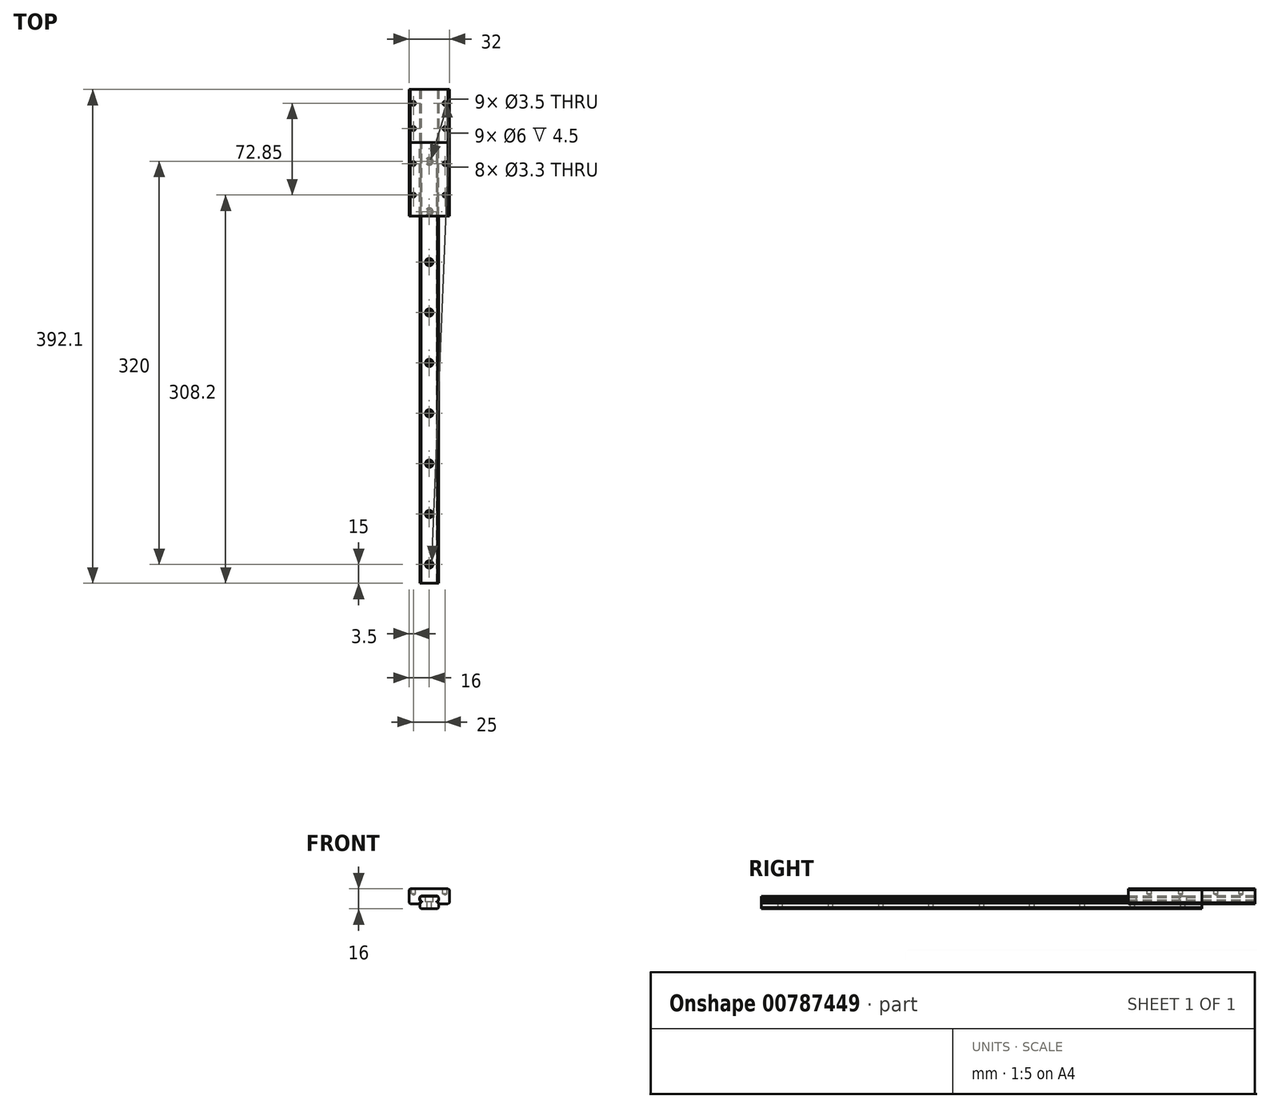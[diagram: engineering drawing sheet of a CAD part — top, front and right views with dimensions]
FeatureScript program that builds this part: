
annotation { "Feature Type Name" : "Feature", "Feature Type Description" : "" }
export const myFeature = defineFeature(function(context is Context, id is Id, definition is map)
    precondition{}
    {
        {
            var Q0;
            Q0=qCreatedBy(makeId("Front.planeOp"),FACE);
            var sketch = newSketch(context, id + "F0", { "sketchPlane" : qUnion([Q0])});
            skLineSegment(sketch, "E0.bottom", {"start": v(6.5, -5) * mm, "end": v(-6.5, -5) * mm});
            skLineSegment(sketch, "E0.top", {"start": v(6.5, 5) * mm, "end": v(-6.5, 5) * mm});
            skLineSegment(sketch, "E0.left", {"start": v(7.5, -4) * mm, "end": v(7.5, -0.41) * mm});
            skLineSegment(sketch, "E0.right", {"start": v(-7.5, -4) * mm, "end": v(-7.5, -0.41) * mm});
            skPoint(sketch, "E0.middle", {"position": v(0, 0) * mm});
            skLineSegment(sketch, "E1", {"start": v(0, 12.36) * mm, "end": v(0, -9.73) * mm, "construction": true});
            skLineSegment(sketch, "E2", {"start": v(-7.5, 2) * mm, "end": v(-6.8, 1.3) * mm});
            skLineSegment(sketch, "E3", {"start": v(-6.8, 1.3) * mm, "end": v(-5.8, 1.3) * mm});
            skLineSegment(sketch, "E4", {"start": v(-5.8, 1.3) * mm, "end": v(-5.8, 0.3) * mm});
            skLineSegment(sketch, "E5", {"start": v(-5.8, 0.3) * mm, "end": v(-6.8, 0.3) * mm});
            skLineSegment(sketch, "E6", {"start": v(-6.8, 0.3) * mm, "end": v(-7.5, -0.41) * mm});
            skLineSegment(sketch, "E7.MirrorCS", {"start": v(5.8, 0.3) * mm, "end": v(6.8, 0.3) * mm});
            skLineSegment(sketch, "E8.MirrorCS", {"start": v(6.8, 0.3) * mm, "end": v(7.5, -0.41) * mm});
            skLineSegment(sketch, "E9.MirrorCS", {"start": v(5.8, 1.3) * mm, "end": v(5.8, 0.3) * mm});
            skLineSegment(sketch, "E10.MirrorCS", {"start": v(7.5, 2) * mm, "end": v(6.8, 1.3) * mm});
            skLineSegment(sketch, "E11.MirrorCS", {"start": v(6.8, 1.3) * mm, "end": v(5.8, 1.3) * mm});
            skLineSegment(sketch, "E12.trimOffspring", {"start": v(-7.5, 2) * mm, "end": v(-7.5, 4) * mm});
            skLineSegment(sketch, "E13.trimOffspring", {"start": v(7.5, 2) * mm, "end": v(7.5, 4) * mm});
            skLineSegment(sketch, "E14", {"start": v(-7.5, 4) * mm, "end": v(-6.5, 5) * mm});
            skLineSegment(sketch, "E15.MirrorCS", {"start": v(7.5, 4) * mm, "end": v(6.5, 5) * mm});
            skLineSegment(sketch, "E16.MirrorCS", {"start": v(-7.5, -4) * mm, "end": v(-6.5, -5) * mm});
            skLineSegment(sketch, "E17.MirrorCS", {"start": v(7.5, -4) * mm, "end": v(6.5, -5) * mm});
            skPoint(sketch, "E18.orphan", {"position": v(-7.5, 5) * mm});
            skPoint(sketch, "E19.orphan", {"position": v(7.5, 5) * mm});
            skPoint(sketch, "E20.orphan", {"position": v(7.5, -5) * mm});
            skPoint(sketch, "E21.orphan", {"position": v(-7.5, -5) * mm});
            skSolve(sketch);
        }
        {
            var Q0;
            Q0=makeQuery(id+"F0.imprint","IMPRINT",FACE,{"disambiguationData":[TD([[makeQuery(id+"F0.imprint","IMPRINT",EDGE,{"derivedFrom":sQuery(id+"F0.wireOp",EDGE,"E0.bottom")}),-1.0]])]});
            extrude(context, id + "F1", {"entities" : qUnion([Q0]), "depth" : 350 * mm, "offsetDistance" : 25 * mm});
        }
        {
            var Q0;
            Q0=makeQuery(id+"F1.opExtrude","SWEPT_FACE",FACE,{"disambiguationData":[OSD([sQuery(id+"F0.wireOp",EDGE,"E0.top")])]});
            var sketch = newSketch(context, id + "F2", { "sketchPlane" : qUnion([Q0])});
            skLineSegment(sketch, "E22", {"start": v(0, 4.61) * mm, "end": v(0, -375.08) * mm, "construction": true});
            skCircle(sketch, "E23", {"center": v(0, -15) * mm, "radius": 1.75 * mm});
            skCircle(sketch, "E24.1.0.0", {"center": v(0, -55) * mm, "radius": 1.75 * mm});
            skCircle(sketch, "E24.2.0.0", {"center": v(0, -95) * mm, "radius": 1.75 * mm});
            skCircle(sketch, "E24.3.0.0", {"center": v(0, -135) * mm, "radius": 1.75 * mm});
            skCircle(sketch, "E24.4.0.0", {"center": v(0, -175) * mm, "radius": 1.75 * mm});
            skCircle(sketch, "E24.5.0.0", {"center": v(0, -215) * mm, "radius": 1.75 * mm});
            skCircle(sketch, "E24.6.0.0", {"center": v(0, -255) * mm, "radius": 1.75 * mm});
            skCircle(sketch, "E24.7.0.0", {"center": v(0, -295) * mm, "radius": 1.75 * mm});
            skCircle(sketch, "E24.8.0.0", {"center": v(0, -335) * mm, "radius": 1.75 * mm});
            skLineSegment(sketch, "E24.direction1", {"start": v(0, -15) * mm, "end": v(0, -55) * mm, "construction": true});
            skSolve(sketch);
        }
        {
            var Q0;
            Q0 = qSketchRegion(id + "F2", true);
            extrude(context, id + "F3", {"entities" : qUnion([Q0]), "operationType" : NewBodyOperationType.REMOVE, "endBound" : BoundingType.THROUGH_ALL, "oppositeDirection" : true, "depth" : 25 * mm, "offsetDistance" : 25 * mm});
        }
        {
            var Q0;
            Q0=makeQuery(id+"F1.opExtrude","SWEPT_FACE",FACE,{"disambiguationData":[OSD([sQuery(id+"F0.wireOp",EDGE,"E0.top")])]});
            var sketch = newSketch(context, id + "F4", { "sketchPlane" : qUnion([Q0])});
            skLineSegment(sketch, "E25", {"start": v(0, 167.82) * mm, "end": v(0, -211.88) * mm, "construction": true});
            skCircle(sketch, "E26", {"center": v(0, -15) * mm, "radius": 3 * mm});
            skCircle(sketch, "E27.1.0.0", {"center": v(0, -55) * mm, "radius": 3 * mm});
            skCircle(sketch, "E27.2.0.0", {"center": v(0, -95) * mm, "radius": 3 * mm});
            skCircle(sketch, "E27.3.0.0", {"center": v(0, -135) * mm, "radius": 3 * mm});
            skCircle(sketch, "E27.4.0.0", {"center": v(0, -175) * mm, "radius": 3 * mm});
            skCircle(sketch, "E27.5.0.0", {"center": v(0, -215) * mm, "radius": 3 * mm});
            skCircle(sketch, "E27.6.0.0", {"center": v(0, -255) * mm, "radius": 3 * mm});
            skCircle(sketch, "E27.7.0.0", {"center": v(0, -295) * mm, "radius": 3 * mm});
            skCircle(sketch, "E27.8.0.0", {"center": v(0, -335) * mm, "radius": 3 * mm});
            skLineSegment(sketch, "E27.direction1", {"start": v(0, -15) * mm, "end": v(0, -55) * mm, "construction": true});
            skSolve(sketch);
        }
        {
            var Q0;
            Q0 = qSketchRegion(id + "F4", true);
            extrude(context, id + "F5", {"entities" : qUnion([Q0]), "operationType" : NewBodyOperationType.REMOVE, "oppositeDirection" : true, "depth" : 4.5 * mm, "offsetDistance" : 25 * mm});
        }
        {
            var Q0;
            Q0=qCreatedBy(makeId("Front.planeOp"),FACE);
            var sketch = newSketch(context, id + "F6", { "sketchPlane" : qUnion([Q0])});
            skLineSegment(sketch, "E28", {"start": v(-7.65, -1) * mm, "end": v(-15, -1) * mm});
            skLineSegment(sketch, "E29", {"start": v(-16, 0) * mm, "end": v(-16, 10) * mm});
            skLineSegment(sketch, "E30", {"start": v(-15, 11) * mm, "end": v(0, 11) * mm});
            skLineSegment(sketch, "E31", {"start": v(-7.65, -1) * mm, "end": v(-7.65, -0.35) * mm});
            skLineSegment(sketch, "E32", {"start": v(-7.65, -0.35) * mm, "end": v(-6.8, 0.5) * mm});
            skLineSegment(sketch, "E33", {"start": v(-6.8, 0.5) * mm, "end": v(-6.8, 1.08) * mm});
            skLineSegment(sketch, "E34", {"start": v(-6.8, 1.08) * mm, "end": v(-7.65, 1.94) * mm});
            skLineSegment(sketch, "E35", {"start": v(-7.65, 1.94) * mm, "end": v(-7.65, 4.06) * mm});
            skLineSegment(sketch, "E36", {"start": v(-7.65, 4.06) * mm, "end": v(-6.56, 5.15) * mm});
            skLineSegment(sketch, "E37", {"start": v(-6.56, 5.15) * mm, "end": v(0, 5.15) * mm});
            skLineSegment(sketch, "E38", {"start": v(-16, 10) * mm, "end": v(-15, 11) * mm});
            skLineSegment(sketch, "E39", {"start": v(-15, -1) * mm, "end": v(-16, 0) * mm});
            skPoint(sketch, "E40.orphan", {"position": v(-16, -1) * mm});
            skPoint(sketch, "E41.orphan", {"position": v(-16, 11) * mm});
            skLineSegment(sketch, "E42.MirrorCS", {"start": v(15, 11) * mm, "end": v(0, 11) * mm});
            skLineSegment(sketch, "E43.MirrorCS", {"start": v(16, 10) * mm, "end": v(15, 11) * mm});
            skLineSegment(sketch, "E44.MirrorCS", {"start": v(16, 0) * mm, "end": v(16, 10) * mm});
            skLineSegment(sketch, "E45.MirrorCS", {"start": v(15, -1) * mm, "end": v(16, 0) * mm});
            skLineSegment(sketch, "E46.MirrorCS", {"start": v(7.65, -1) * mm, "end": v(15, -1) * mm});
            skLineSegment(sketch, "E47.MirrorCS", {"start": v(7.65, -1) * mm, "end": v(7.65, -0.35) * mm});
            skLineSegment(sketch, "E48.MirrorCS", {"start": v(7.65, -0.35) * mm, "end": v(6.8, 0.5) * mm});
            skLineSegment(sketch, "E49.MirrorCS", {"start": v(6.8, 0.5) * mm, "end": v(6.8, 1.08) * mm});
            skLineSegment(sketch, "E50.MirrorCS", {"start": v(6.8, 1.08) * mm, "end": v(7.65, 1.94) * mm});
            skLineSegment(sketch, "E51.MirrorCS", {"start": v(7.65, 1.94) * mm, "end": v(7.65, 4.06) * mm});
            skLineSegment(sketch, "E52.MirrorCS", {"start": v(7.65, 4.06) * mm, "end": v(6.56, 5.15) * mm});
            skLineSegment(sketch, "E53.MirrorCS", {"start": v(6.56, 5.15) * mm, "end": v(0, 5.15) * mm});
            skSolve(sketch);
        }
        {
            var Q0;
            Q0 = qSketchRegion(id + "F6", true);
            extrude(context, id + "F7", {"entities" : qUnion([Q0]), "depth" : 58.6 * mm, "offsetDistance" : 25 * mm});
        }
        {
            var Q0;
            Q0 = qSketchRegion(id + "F6", true);
            extrude(context, id + "F8", {"entities" : qUnion([Q0]), "oppositeDirection" : true, "depth" : 42.1 * mm, "offsetDistance" : 25 * mm});
        }
        {
            var Q0;
            Q0=makeQuery(id+"F7.opExtrude","SWEPT_FACE",FACE,{"disambiguationData":[OSD([sQuery(id+"F6.wireOp",EDGE,"E30"),sQuery(id+"F6.wireOp",EDGE,"E42.MirrorCS")])]});
            var sketch = newSketch(context, id + "F9", { "sketchPlane" : qUnion([Q0])});
            skLineSegment(sketch, "E54", {"start": v(-15, 0) * mm, "end": v(15, -58.6) * mm, "construction": true});
            skLineSegment(sketch, "E55", {"start": v(15, 0) * mm, "end": v(-15, -58.6) * mm, "construction": true});
            skLineSegment(sketch, "E56", {"start": v(-37.81, -29.3) * mm, "end": v(32.35, -29.3) * mm, "construction": true});
            skPoint(sketch, "E56.startSnap0", {"position": v(0, -29.3) * mm});
            skLineSegment(sketch, "E57", {"start": v(0, 0) * mm, "end": v(0, -61.52) * mm, "construction": true});
            skCircle(sketch, "E58", {"center": v(-12.5, -16.8) * mm, "radius": 1.5 * mm});
            skCircle(sketch, "E59.MirrorC", {"center": v(12.5, -16.8) * mm, "radius": 1.5 * mm});
            skCircle(sketch, "E60.MirrorC", {"center": v(-12.5, -41.8) * mm, "radius": 1.5 * mm});
            skCircle(sketch, "E61.MirrorC", {"center": v(12.5, -41.8) * mm, "radius": 1.5 * mm});
            skSolve(sketch);
        }
        {
            var Q0;
            Q0=makeQuery(id+"F8.opExtrude","SWEPT_FACE",FACE,{"disambiguationData":[OSD([sQuery(id+"F6.wireOp",EDGE,"E30"),sQuery(id+"F6.wireOp",EDGE,"E42.MirrorCS")])]});
            var sketch = newSketch(context, id + "F10", { "sketchPlane" : qUnion([Q0])});
            skLineSegment(sketch, "E62", {"start": v(-34.35, 21.05) * mm, "end": v(28.23, 21.05) * mm, "construction": true});
            skLineSegment(sketch, "E63", {"start": v(0, 49.38) * mm, "end": v(0, -1.77) * mm, "construction": true});
            skCircle(sketch, "E64", {"center": v(-12.5, 31.05) * mm, "radius": 1.5 * mm});
            skCircle(sketch, "E65.MirrorC", {"center": v(12.5, 31.05) * mm, "radius": 1.5 * mm});
            skCircle(sketch, "E66.MirrorC", {"center": v(-12.5, 11.05) * mm, "radius": 1.5 * mm});
            skCircle(sketch, "E67.MirrorC", {"center": v(12.5, 11.05) * mm, "radius": 1.5 * mm});
            skSolve(sketch);
        }
        {
            var Q0;
            Q0=sQuery(id+"F9.wireOp",VERTEX,"E58.center");
            var Q1;
            Q1=sQuery(id+"F9.wireOp",VERTEX,"E59.MirrorC.center");
            var Q2;
            Q2=sQuery(id+"F9.wireOp",VERTEX,"E60.MirrorC.center");
            var Q3;
            Q3=sQuery(id+"F9.wireOp",VERTEX,"E61.MirrorC.center");
            var Q4;
            Q4=makeQuery(id+"F7.opExtrude","SWEPT_BODY",BODY,{"disambiguationData":[OSD([sQuery(id+"F6.wireOp",EDGE,"E28"),sQuery(id+"F6.wireOp",EDGE,"E29"),sQuery(id+"F6.wireOp",EDGE,"E30"),sQuery(id+"F6.wireOp",EDGE,"E31"),sQuery(id+"F6.wireOp",EDGE,"E32"),sQuery(id+"F6.wireOp",EDGE,"E33"),sQuery(id+"F6.wireOp",EDGE,"E34"),sQuery(id+"F6.wireOp",EDGE,"E35"),sQuery(id+"F6.wireOp",EDGE,"E36"),sQuery(id+"F6.wireOp",EDGE,"E37"),sQuery(id+"F6.wireOp",EDGE,"E38"),sQuery(id+"F6.wireOp",EDGE,"E39"),sQuery(id+"F6.wireOp",EDGE,"E42.MirrorCS"),sQuery(id+"F6.wireOp",EDGE,"E43.MirrorCS"),sQuery(id+"F6.wireOp",EDGE,"E44.MirrorCS"),sQuery(id+"F6.wireOp",EDGE,"E45.MirrorCS"),sQuery(id+"F6.wireOp",EDGE,"E46.MirrorCS"),sQuery(id+"F6.wireOp",EDGE,"E47.MirrorCS"),sQuery(id+"F6.wireOp",EDGE,"E48.MirrorCS"),sQuery(id+"F6.wireOp",EDGE,"E49.MirrorCS"),sQuery(id+"F6.wireOp",EDGE,"E50.MirrorCS"),sQuery(id+"F6.wireOp",EDGE,"E51.MirrorCS"),sQuery(id+"F6.wireOp",EDGE,"E52.MirrorCS"),sQuery(id+"F6.wireOp",EDGE,"E53.MirrorCS")])]});
            hole(context, id + "F11", {"style" : HoleStyle.SIMPLE, "endStyle" : HoleEndStyle.BLIND, "standardTappedOrClearance" : lookupTablePath({ "standard" : "ISO", "fit" : "Normal", "size" : "M3", "type" : "Clearance" }), "standardBlindInLast" : lookupTablePath({ "fit" : "Standard", "standard" : "ISO", "size" : "M3", "type" : "Clearance" }), "holeDiameter" : 3.3 * mm, "majorDiameter" : 5 * mm, "holeDepth" : 4 * mm, "isTappedThrough" : true, "tappedDepth" : 12 * mm, "tapClearance" : 3, "startFromSketch" : true, "locations" : qUnion([Q0, Q1, Q2, Q3]), "scope" : qUnion([Q4])});
        }
        {
            var Q0;
            Q0=sQuery(id+"F10.wireOp",VERTEX,"E64.center");
            var Q1;
            Q1=sQuery(id+"F10.wireOp",VERTEX,"E65.MirrorC.center");
            var Q2;
            Q2=sQuery(id+"F10.wireOp",VERTEX,"E67.MirrorC.center");
            var Q3;
            Q3=sQuery(id+"F10.wireOp",VERTEX,"E66.MirrorC.center");
            var Q4;
            Q4=makeQuery(id+"F8.opExtrude","SWEPT_BODY",BODY,{"disambiguationData":[OSD([sQuery(id+"F6.wireOp",EDGE,"E28"),sQuery(id+"F6.wireOp",EDGE,"E29"),sQuery(id+"F6.wireOp",EDGE,"E30"),sQuery(id+"F6.wireOp",EDGE,"E31"),sQuery(id+"F6.wireOp",EDGE,"E32"),sQuery(id+"F6.wireOp",EDGE,"E33"),sQuery(id+"F6.wireOp",EDGE,"E34"),sQuery(id+"F6.wireOp",EDGE,"E35"),sQuery(id+"F6.wireOp",EDGE,"E36"),sQuery(id+"F6.wireOp",EDGE,"E37"),sQuery(id+"F6.wireOp",EDGE,"E38"),sQuery(id+"F6.wireOp",EDGE,"E39"),sQuery(id+"F6.wireOp",EDGE,"E42.MirrorCS"),sQuery(id+"F6.wireOp",EDGE,"E43.MirrorCS"),sQuery(id+"F6.wireOp",EDGE,"E44.MirrorCS"),sQuery(id+"F6.wireOp",EDGE,"E45.MirrorCS"),sQuery(id+"F6.wireOp",EDGE,"E46.MirrorCS"),sQuery(id+"F6.wireOp",EDGE,"E47.MirrorCS"),sQuery(id+"F6.wireOp",EDGE,"E48.MirrorCS"),sQuery(id+"F6.wireOp",EDGE,"E49.MirrorCS"),sQuery(id+"F6.wireOp",EDGE,"E50.MirrorCS"),sQuery(id+"F6.wireOp",EDGE,"E51.MirrorCS"),sQuery(id+"F6.wireOp",EDGE,"E52.MirrorCS"),sQuery(id+"F6.wireOp",EDGE,"E53.MirrorCS")])]});
            hole(context, id + "F12", {"style" : HoleStyle.SIMPLE, "endStyle" : HoleEndStyle.BLIND, "standardTappedOrClearance" : lookupTablePath({ "standard" : "ISO", "fit" : "Normal", "size" : "M3", "type" : "Clearance" }), "standardBlindInLast" : lookupTablePath({ "fit" : "Standard", "standard" : "ISO", "size" : "M3", "type" : "Clearance" }), "holeDiameter" : 3.3 * mm, "majorDiameter" : 5 * mm, "holeDepth" : 4 * mm, "isTappedThrough" : true, "tappedDepth" : 12 * mm, "tapClearance" : 3, "startFromSketch" : true, "locations" : qUnion([Q0, Q1, Q2, Q3]), "scope" : qUnion([Q4])});
        }
    });
